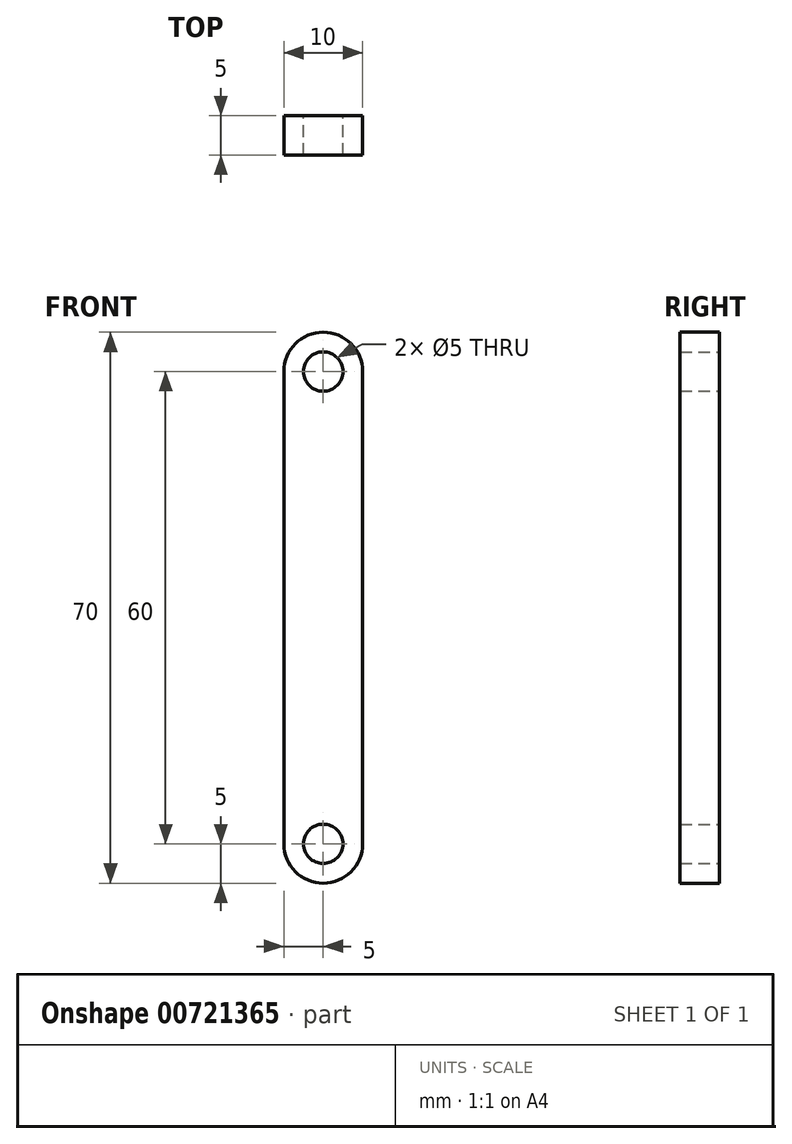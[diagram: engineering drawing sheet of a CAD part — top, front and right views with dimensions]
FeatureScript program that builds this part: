
annotation { "Feature Type Name" : "Feature", "Feature Type Description" : "" }
export const myFeature = defineFeature(function(context is Context, id is Id, definition is map)
    precondition{}
    {
        {
            var Q0;
            Q0=qCreatedBy(makeId("Front.planeOp"),FACE);
            var sketch = newSketch(context, id + "F0", { "sketchPlane" : qUnion([Q0])});
            skLineSegment(sketch, "E0.left", {"start": v(5, 30) * mm, "end": v(5, -30) * mm});
            skLineSegment(sketch, "E0.right", {"start": v(-5, 30) * mm, "end": v(-5, -30) * mm});
            skPoint(sketch, "E0.middle", {"position": v(0, 0) * mm});
            skArc(sketch, "E1", {"start": v(5, 30) * mm, "mid": v(0, 35) * mm, "end": v(-5, 30) * mm});
            skArc(sketch, "E2", {"start": v(-5, -30) * mm, "mid": v(0, -35) * mm, "end": v(5, -30) * mm});
            skCircle(sketch, "E3", {"center": v(0, 30) * mm, "radius": 2.5 * mm});
            skCircle(sketch, "E4", {"center": v(0, -30) * mm, "radius": 2.5 * mm});
            skSolve(sketch);
        }
        {
            var Q0;
            Q0 = qSketchRegion(id + "F0", true);
            extrude(context, id + "F1", {"entities" : qUnion([Q0]), "depth" : 5 * mm, "offsetDistance" : 25.4 * mm});
        }
    });
